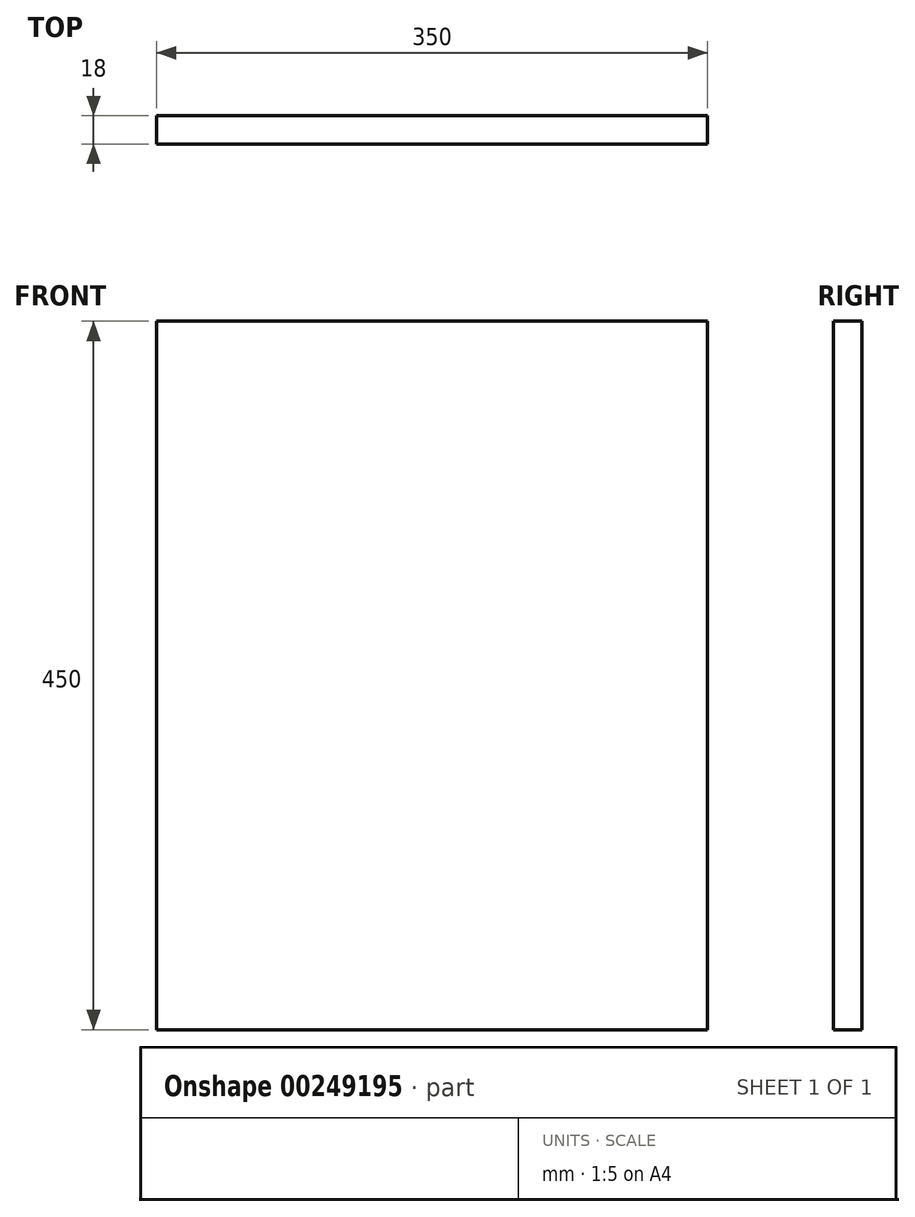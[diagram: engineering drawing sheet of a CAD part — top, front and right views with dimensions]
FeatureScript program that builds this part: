
annotation { "Feature Type Name" : "Feature", "Feature Type Description" : "" }
export const myFeature = defineFeature(function(context is Context, id is Id, definition is map)
    precondition{}
    {
        {
            var Q0;
            Q0=qCreatedBy(makeId("Front.planeOp"),FACE);
            var sketch = newSketch(context, id + "F0", { "sketchPlane" : qUnion([Q0])});
            skLineSegment(sketch, "E0.bottom", {"start": v(175, 225) * mm, "end": v(-175, 225) * mm});
            skLineSegment(sketch, "E0.top", {"start": v(175, -225) * mm, "end": v(-175, -225) * mm});
            skLineSegment(sketch, "E0.left", {"start": v(175, 225) * mm, "end": v(175, -225) * mm});
            skLineSegment(sketch, "E0.right", {"start": v(-175, 225) * mm, "end": v(-175, -225) * mm});
            skPoint(sketch, "E0.middle", {"position": v(0, 0) * mm});
            skSolve(sketch);
        }
        {
            var Q0;
            Q0 = qSketchRegion(id + "F0", true);
            extrude(context, id + "F1", {"entities" : qUnion([Q0]), "depth" : 18 * mm});
        }
    });
